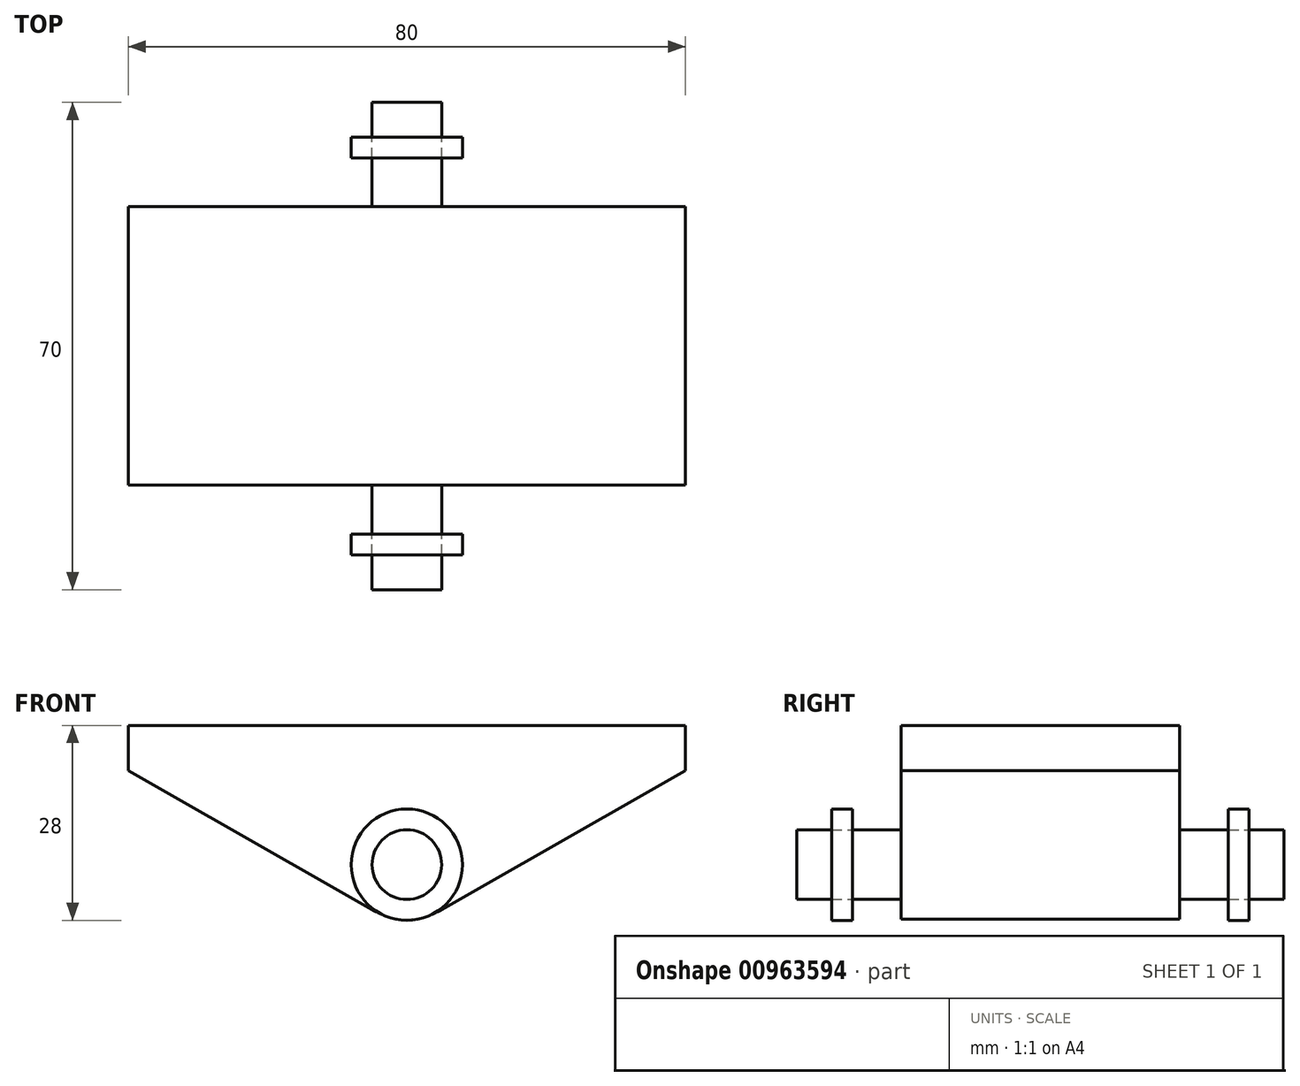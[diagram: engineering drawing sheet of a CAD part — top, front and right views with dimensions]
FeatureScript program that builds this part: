
annotation { "Feature Type Name" : "Feature", "Feature Type Description" : "" }
export const myFeature = defineFeature(function(context is Context, id is Id, definition is map)
    precondition{}
    {
        {
            var Q0;
            Q0=qCreatedBy(makeId("Front.planeOp"),FACE);
            var sketch = newSketch(context, id + "F0", { "sketchPlane" : qUnion([Q0])});
            skCircle(sketch, "E0", {"center": v(0, 0) * mm, "radius": 5 * mm});
            skLineSegment(sketch, "E1", {"start": v(-70, 50) * mm, "end": v(-70, -50) * mm, "construction": true});
            skLineSegment(sketch, "E2", {"start": v(-70, -50) * mm, "end": v(70, -50) * mm, "construction": true});
            skLineSegment(sketch, "E3", {"start": v(70, -50) * mm, "end": v(70, 0) * mm, "construction": true});
            skLineSegment(sketch, "E4", {"start": v(0, 0) * mm, "end": v(-70, 0) * mm, "construction": true});
            skLineSegment(sketch, "E5", {"start": v(-70, 50) * mm, "end": v(70, 50) * mm, "construction": true});
            skLineSegment(sketch, "E6", {"start": v(70, 50) * mm, "end": v(70, 0) * mm, "construction": true});
            skLineSegment(sketch, "E7", {"start": v(0, 0) * mm, "end": v(0, 50) * mm, "construction": true});
            skLineSegment(sketch, "E8", {"start": v(0, 20) * mm, "end": v(-40, 20) * mm});
            skLineSegment(sketch, "E9", {"start": v(-40, 20) * mm, "end": v(-40, 13.5) * mm});
            skLineSegment(sketch, "E10", {"start": v(-40, 13.5) * mm, "end": v(-4.96, -6.5) * mm});
            skLineSegment(sketch, "E11.MirrorCS", {"start": v(0, 20) * mm, "end": v(40, 20) * mm});
            skLineSegment(sketch, "E12.MirrorCS", {"start": v(40, 20) * mm, "end": v(40, 13.5) * mm});
            skLineSegment(sketch, "E13.MirrorCS", {"start": v(40, 13.5) * mm, "end": v(4.96, -6.5) * mm});
            skPoint(sketch, "E14.visualSharp", {"position": v(0, -9.34) * mm});
            skArc(sketch, "E14.filletArc", {"start": v(-4.96, -6.5) * mm, "mid": v(0, -7.82) * mm, "end": v(4.96, -6.5) * mm});
            skSolve(sketch);
        }
        {
            var Q0;
            Q0=makeQuery(id+"F0.imprint","IMPRINT",FACE,{"disambiguationData":[TD([[makeQuery(id+"F0.imprint","IMPRINT",EDGE,{"derivedFrom":sQuery(id+"F0.wireOp",EDGE,"E0")}),-1.0]])]});
            extrude(context, id + "F1", {"entities" : qUnion([Q0]), "endBound" : BoundingType.SYMMETRIC, "depth" : 40 * mm, "offsetDistance" : 25 * mm});
        }
        {
            var Q0;
            Q0=makeQuery(id+"F0.imprint","IMPRINT",FACE,{"disambiguationData":[TD([[makeQuery(id+"F0.imprint","IMPRINT",EDGE,{"derivedFrom":sQuery(id+"F0.wireOp",EDGE,"E0")}),1.0]])]});
            extrude(context, id + "F2", {"entities" : qUnion([Q0]), "operationType" : NewBodyOperationType.ADD, "endBound" : BoundingType.SYMMETRIC, "depth" : 70 * mm, "offsetDistance" : 25 * mm});
        }
        {
            var Q0;
            Q0=qCreatedBy(makeId("Front.planeOp"),FACE);
            cPlane(context, id + "F3", {"entities" : qUnion([Q0]), "cplaneType" : CPlaneType.OFFSET, "offset" : 27 * mm, "width" : 150 * mm, "height" : 150 * mm});
        }
        {
            var Q0;
            Q0=qCreatedBy(id+"F3.planeOp",FACE);
            var sketch = newSketch(context, id + "F4", { "sketchPlane" : qUnion([Q0])});
            skPoint(sketch, "E15.0", {"position": v(0, 0) * mm});
            skCircle(sketch, "E16", {"center": v(0, 0) * mm, "radius": 8 * mm});
            skSolve(sketch);
        }
        {
            var Q0;
            Q0=makeQuery(id+"F4.imprint","IMPRINT",FACE,{"disambiguationData":[TD([[makeQuery(id+"F4.imprint","IMPRINT",EDGE,{"derivedFrom":sQuery(id+"F4.wireOp",EDGE,"E16")}),1.0]])]});
            extrude(context, id + "F5", {"entities" : qUnion([Q0]), "depth" : 3 * mm, "offsetDistance" : 25 * mm});
        }
        {
            var Q0;
            Q0=makeQuery(id+"F5.opExtrude","SWEPT_BODY",BODY,{"disambiguationData":[OSD([sQuery(id+"F4.wireOp",EDGE,"E16")])]});
            var Q1;
            Q1=qCreatedBy(makeId("Front.planeOp"),FACE);
            mirror(context, id + "F6", {"entities" : qUnion([Q0]), "mirrorPlane" : qUnion([Q1])});
        }
    });
